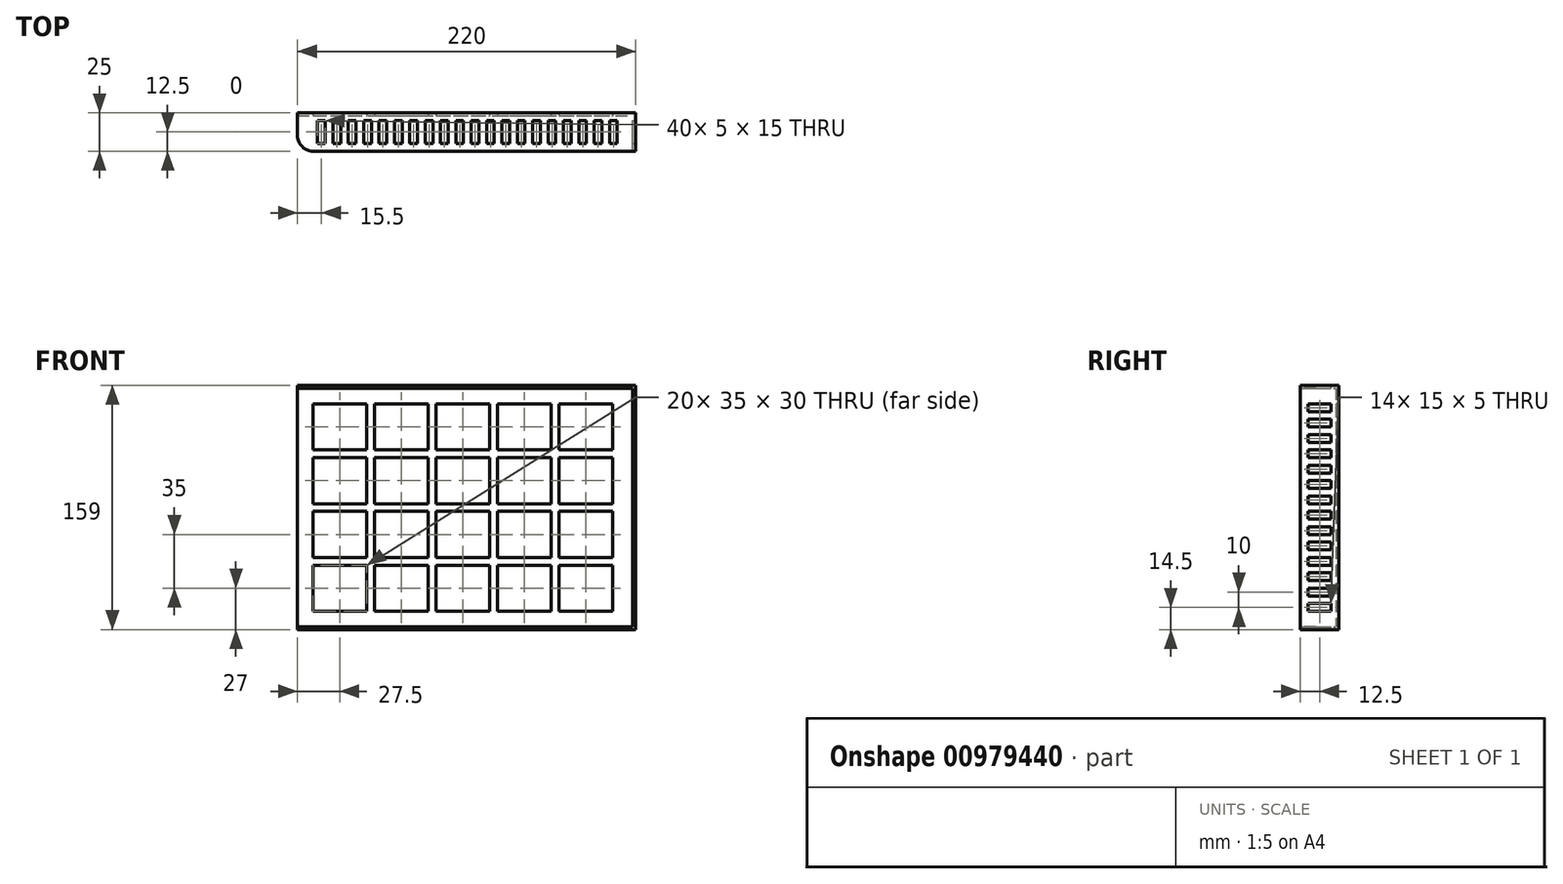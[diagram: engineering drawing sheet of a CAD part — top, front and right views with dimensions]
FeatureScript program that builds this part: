
annotation { "Feature Type Name" : "Feature", "Feature Type Description" : "" }
export const myFeature = defineFeature(function(context is Context, id is Id, definition is map)
    precondition{}
    {
        {
            var Q0;
            Q0=qCreatedBy(makeId("Front.planeOp"),FACE);
            var sketch = newSketch(context, id + "F0", { "sketchPlane" : qUnion([Q0])});
            skLineSegment(sketch, "E0.bottom", {"start": v(-110, 79.5) * mm, "end": v(110, 79.5) * mm});
            skLineSegment(sketch, "E0.top", {"start": v(-110, -79.5) * mm, "end": v(110, -79.5) * mm});
            skLineSegment(sketch, "E0.left", {"start": v(-110, 79.5) * mm, "end": v(-110, -79.5) * mm});
            skLineSegment(sketch, "E0.right", {"start": v(110, 79.5) * mm, "end": v(110, -79.5) * mm});
            skSolve(sketch);
        }
        {
            var Q0;
            Q0 = qSketchRegion(id + "F0", true);
            extrude(context, id + "F1", {"entities" : qUnion([Q0]), "depth" : 25 * mm, "offsetDistance" : 25 * mm});
        }
        {
            var Q0;
            Q0=makeQuery(id+"F1.opExtrude","CAP_FACE",FACE,{"disambiguationData":[OSD([sQuery(id+"F0.wireOp",EDGE,"E0.bottom"),sQuery(id+"F0.wireOp",EDGE,"E0.top"),sQuery(id+"F0.wireOp",EDGE,"E0.left"),sQuery(id+"F0.wireOp",EDGE,"E0.right")])],"isStart":false});
            var Q1;
            Q1=makeQuery(id+"F1.opExtrude","SWEPT_FACE",FACE,{"disambiguationData":[OSD([sQuery(id+"F0.wireOp",EDGE,"E0.left")])]});
            shell(context, id + "F2", {"entities" : qUnion([Q0, Q1]), "thickness" : 2 * mm});
        }
        {
            var Q0;
            {var subQ0=sQuery(id+"F0.wireOp",EDGE,"E0.left");Q0=makeQuery(id+"F2.opShell","OFFSET_EDGE",EDGE,{"disambiguationData":[OSD([subQ0]),TDD([makeQuery(id+"F1.opExtrude","CAP_EDGE",EDGE,{"disambiguationData":[OSD([subQ0])],"isStart":false})])]});}
            fillet(context, id + "F3", {"entities" : qUnion([Q0]), "radius" : 10 * mm, "tangentPropagation" : true, "allowEdgeOverflow" : false});
        }
        {
            var Q0;
            Q0=makeQuery(id+"F1.opExtrude","CAP_EDGE",EDGE,{"disambiguationData":[OSD([sQuery(id+"F0.wireOp",EDGE,"E0.left")])],"isStart":false});
            fillet(context, id + "F4", {"entities" : qUnion([Q0]), "radius" : 10 * mm, "tangentPropagation" : true, "allowEdgeOverflow" : false});
        }
        {
            var Q0;
            Q0=makeQuery(id+"F2.opShell","OFFSET_FACE",FACE,{"disambiguationData":[OSD([sQuery(id+"F0.wireOp",EDGE,"E0.bottom"),sQuery(id+"F0.wireOp",EDGE,"E0.top"),sQuery(id+"F0.wireOp",EDGE,"E0.left"),sQuery(id+"F0.wireOp",EDGE,"E0.right")])]});
            var sketch = newSketch(context, id + "F5", { "sketchPlane" : qUnion([Q0])});
            skLineSegment(sketch, "E1.bottom", {"start": v(-110, 77.5) * mm, "end": v(-100, 77.5) * mm});
            skLineSegment(sketch, "E1.top", {"start": v(-110, 67.5) * mm, "end": v(-100, 67.5) * mm});
            skLineSegment(sketch, "E1.left", {"start": v(-110, 77.5) * mm, "end": v(-110, 67.5) * mm});
            skLineSegment(sketch, "E1.right", {"start": v(-100, 77.5) * mm, "end": v(-100, 67.5) * mm});
            skLineSegment(sketch, "E2.bottom", {"start": v(-100, 67.5) * mm, "end": v(-65, 67.5) * mm});
            skLineSegment(sketch, "E2.top", {"start": v(-100, 37.5) * mm, "end": v(-65, 37.5) * mm});
            skLineSegment(sketch, "E2.left", {"start": v(-100, 67.5) * mm, "end": v(-100, 37.5) * mm});
            skLineSegment(sketch, "E2.right", {"start": v(-65, 67.5) * mm, "end": v(-65, 37.5) * mm});
            skLineSegment(sketch, "E3.0.1.0", {"start": v(-65, 32.5) * mm, "end": v(-65, 2.5) * mm});
            skLineSegment(sketch, "E3.0.1.1", {"start": v(-100, 32.5) * mm, "end": v(-65, 32.5) * mm});
            skLineSegment(sketch, "E3.0.1.2", {"start": v(-100, 32.5) * mm, "end": v(-100, 2.5) * mm});
            skLineSegment(sketch, "E3.0.1.3", {"start": v(-100, 2.5) * mm, "end": v(-65, 2.5) * mm});
            skLineSegment(sketch, "E3.0.2.0", {"start": v(-65, -2.5) * mm, "end": v(-65, -32.5) * mm});
            skLineSegment(sketch, "E3.0.2.1", {"start": v(-100, -2.5) * mm, "end": v(-65, -2.5) * mm});
            skLineSegment(sketch, "E3.0.2.2", {"start": v(-100, -2.5) * mm, "end": v(-100, -32.5) * mm});
            skLineSegment(sketch, "E3.0.2.3", {"start": v(-100, -32.5) * mm, "end": v(-65, -32.5) * mm});
            skLineSegment(sketch, "E3.0.3.0", {"start": v(-65, -37.5) * mm, "end": v(-65, -67.5) * mm});
            skLineSegment(sketch, "E3.0.3.1", {"start": v(-100, -37.5) * mm, "end": v(-65, -37.5) * mm});
            skLineSegment(sketch, "E3.0.3.2", {"start": v(-100, -37.5) * mm, "end": v(-100, -67.5) * mm});
            skLineSegment(sketch, "E3.0.3.3", {"start": v(-100, -67.5) * mm, "end": v(-65, -67.5) * mm});
            skLineSegment(sketch, "E3.1.0.0", {"start": v(-25, 67.5) * mm, "end": v(-25, 37.5) * mm});
            skLineSegment(sketch, "E3.1.0.1", {"start": v(-60, 67.5) * mm, "end": v(-25, 67.5) * mm});
            skLineSegment(sketch, "E3.1.0.2", {"start": v(-60, 67.5) * mm, "end": v(-60, 37.5) * mm});
            skLineSegment(sketch, "E3.1.0.3", {"start": v(-60, 37.5) * mm, "end": v(-25, 37.5) * mm});
            skLineSegment(sketch, "E3.1.1.0", {"start": v(-25, 32.5) * mm, "end": v(-25, 2.5) * mm});
            skLineSegment(sketch, "E3.1.1.1", {"start": v(-60, 32.5) * mm, "end": v(-25, 32.5) * mm});
            skLineSegment(sketch, "E3.1.1.2", {"start": v(-60, 32.5) * mm, "end": v(-60, 2.5) * mm});
            skLineSegment(sketch, "E3.1.1.3", {"start": v(-60, 2.5) * mm, "end": v(-25, 2.5) * mm});
            skLineSegment(sketch, "E3.1.2.0", {"start": v(-25, -2.5) * mm, "end": v(-25, -32.5) * mm});
            skLineSegment(sketch, "E3.1.2.1", {"start": v(-60, -2.5) * mm, "end": v(-25, -2.5) * mm});
            skLineSegment(sketch, "E3.1.2.2", {"start": v(-60, -2.5) * mm, "end": v(-60, -32.5) * mm});
            skLineSegment(sketch, "E3.1.2.3", {"start": v(-60, -32.5) * mm, "end": v(-25, -32.5) * mm});
            skLineSegment(sketch, "E3.1.3.0", {"start": v(-25, -37.5) * mm, "end": v(-25, -67.5) * mm});
            skLineSegment(sketch, "E3.1.3.1", {"start": v(-60, -37.5) * mm, "end": v(-25, -37.5) * mm});
            skLineSegment(sketch, "E3.1.3.2", {"start": v(-60, -37.5) * mm, "end": v(-60, -67.5) * mm});
            skLineSegment(sketch, "E3.1.3.3", {"start": v(-60, -67.5) * mm, "end": v(-25, -67.5) * mm});
            skLineSegment(sketch, "E3.2.0.0", {"start": v(15, 67.5) * mm, "end": v(15, 37.5) * mm});
            skLineSegment(sketch, "E3.2.0.1", {"start": v(-20, 67.5) * mm, "end": v(15, 67.5) * mm});
            skLineSegment(sketch, "E3.2.0.2", {"start": v(-20, 67.5) * mm, "end": v(-20, 37.5) * mm});
            skLineSegment(sketch, "E3.2.0.3", {"start": v(-20, 37.5) * mm, "end": v(15, 37.5) * mm});
            skLineSegment(sketch, "E3.2.1.0", {"start": v(15, 32.5) * mm, "end": v(15, 2.5) * mm});
            skLineSegment(sketch, "E3.2.1.1", {"start": v(-20, 32.5) * mm, "end": v(15, 32.5) * mm});
            skLineSegment(sketch, "E3.2.1.2", {"start": v(-20, 32.5) * mm, "end": v(-20, 2.5) * mm});
            skLineSegment(sketch, "E3.2.1.3", {"start": v(-20, 2.5) * mm, "end": v(15, 2.5) * mm});
            skLineSegment(sketch, "E3.2.2.0", {"start": v(15, -2.5) * mm, "end": v(15, -32.5) * mm});
            skLineSegment(sketch, "E3.2.2.1", {"start": v(-20, -2.5) * mm, "end": v(15, -2.5) * mm});
            skLineSegment(sketch, "E3.2.2.2", {"start": v(-20, -2.5) * mm, "end": v(-20, -32.5) * mm});
            skLineSegment(sketch, "E3.2.2.3", {"start": v(-20, -32.5) * mm, "end": v(15, -32.5) * mm});
            skLineSegment(sketch, "E3.2.3.0", {"start": v(15, -37.5) * mm, "end": v(15, -67.5) * mm});
            skLineSegment(sketch, "E3.2.3.1", {"start": v(-20, -37.5) * mm, "end": v(15, -37.5) * mm});
            skLineSegment(sketch, "E3.2.3.2", {"start": v(-20, -37.5) * mm, "end": v(-20, -67.5) * mm});
            skLineSegment(sketch, "E3.2.3.3", {"start": v(-20, -67.5) * mm, "end": v(15, -67.5) * mm});
            skLineSegment(sketch, "E3.3.0.0", {"start": v(55, 67.5) * mm, "end": v(55, 37.5) * mm});
            skLineSegment(sketch, "E3.3.0.1", {"start": v(20, 67.5) * mm, "end": v(55, 67.5) * mm});
            skLineSegment(sketch, "E3.3.0.2", {"start": v(20, 67.5) * mm, "end": v(20, 37.5) * mm});
            skLineSegment(sketch, "E3.3.0.3", {"start": v(20, 37.5) * mm, "end": v(55, 37.5) * mm});
            skLineSegment(sketch, "E3.3.1.0", {"start": v(55, 32.5) * mm, "end": v(55, 2.5) * mm});
            skLineSegment(sketch, "E3.3.1.1", {"start": v(20, 32.5) * mm, "end": v(55, 32.5) * mm});
            skLineSegment(sketch, "E3.3.1.2", {"start": v(20, 32.5) * mm, "end": v(20, 2.5) * mm});
            skLineSegment(sketch, "E3.3.1.3", {"start": v(20, 2.5) * mm, "end": v(55, 2.5) * mm});
            skLineSegment(sketch, "E3.3.2.0", {"start": v(55, -2.5) * mm, "end": v(55, -32.5) * mm});
            skLineSegment(sketch, "E3.3.2.1", {"start": v(20, -2.5) * mm, "end": v(55, -2.5) * mm});
            skLineSegment(sketch, "E3.3.2.2", {"start": v(20, -2.5) * mm, "end": v(20, -32.5) * mm});
            skLineSegment(sketch, "E3.3.2.3", {"start": v(20, -32.5) * mm, "end": v(55, -32.5) * mm});
            skLineSegment(sketch, "E3.3.3.0", {"start": v(55, -37.5) * mm, "end": v(55, -67.5) * mm});
            skLineSegment(sketch, "E3.3.3.1", {"start": v(20, -37.5) * mm, "end": v(55, -37.5) * mm});
            skLineSegment(sketch, "E3.3.3.2", {"start": v(20, -37.5) * mm, "end": v(20, -67.5) * mm});
            skLineSegment(sketch, "E3.3.3.3", {"start": v(20, -67.5) * mm, "end": v(55, -67.5) * mm});
            skLineSegment(sketch, "E3.4.0.0", {"start": v(95, 67.5) * mm, "end": v(95, 37.5) * mm});
            skLineSegment(sketch, "E3.4.0.1", {"start": v(60, 67.5) * mm, "end": v(95, 67.5) * mm});
            skLineSegment(sketch, "E3.4.0.2", {"start": v(60, 67.5) * mm, "end": v(60, 37.5) * mm});
            skLineSegment(sketch, "E3.4.0.3", {"start": v(60, 37.5) * mm, "end": v(95, 37.5) * mm});
            skLineSegment(sketch, "E3.4.1.0", {"start": v(95, 32.5) * mm, "end": v(95, 2.5) * mm});
            skLineSegment(sketch, "E3.4.1.1", {"start": v(60, 32.5) * mm, "end": v(95, 32.5) * mm});
            skLineSegment(sketch, "E3.4.1.2", {"start": v(60, 32.5) * mm, "end": v(60, 2.5) * mm});
            skLineSegment(sketch, "E3.4.1.3", {"start": v(60, 2.5) * mm, "end": v(95, 2.5) * mm});
            skLineSegment(sketch, "E3.4.2.0", {"start": v(95, -2.5) * mm, "end": v(95, -32.5) * mm});
            skLineSegment(sketch, "E3.4.2.1", {"start": v(60, -2.5) * mm, "end": v(95, -2.5) * mm});
            skLineSegment(sketch, "E3.4.2.2", {"start": v(60, -2.5) * mm, "end": v(60, -32.5) * mm});
            skLineSegment(sketch, "E3.4.2.3", {"start": v(60, -32.5) * mm, "end": v(95, -32.5) * mm});
            skLineSegment(sketch, "E3.4.3.0", {"start": v(95, -37.5) * mm, "end": v(95, -67.5) * mm});
            skLineSegment(sketch, "E3.4.3.1", {"start": v(60, -37.5) * mm, "end": v(95, -37.5) * mm});
            skLineSegment(sketch, "E3.4.3.2", {"start": v(60, -37.5) * mm, "end": v(60, -67.5) * mm});
            skLineSegment(sketch, "E3.4.3.3", {"start": v(60, -67.5) * mm, "end": v(95, -67.5) * mm});
            skLineSegment(sketch, "E3.direction1", {"start": v(-76, 43.5) * mm, "end": v(-36, 43.5) * mm, "construction": true});
            skLineSegment(sketch, "E3.direction2", {"start": v(-76, 43.5) * mm, "end": v(-76, 8.5) * mm, "construction": true});
            skSolve(sketch);
        }
        {
            var Q0;
            Q0=makeQuery(id+"F5.imprint","IMPRINT",FACE,{"disambiguationData":[TD([[makeQuery(id+"F5.imprint","IMPRINT",EDGE,{"derivedFrom":sQuery(id+"F5.wireOp",EDGE,"E2.bottom")}),-1.0]])]});
            var Q1;
            Q1=makeQuery(id+"F5.imprint","IMPRINT",FACE,{"disambiguationData":[TD([[makeQuery(id+"F5.imprint","IMPRINT",EDGE,{"derivedFrom":sQuery(id+"F5.wireOp",EDGE,"E3.1.0.0")}),-1.0]])]});
            var Q2;
            Q2=makeQuery(id+"F5.imprint","IMPRINT",FACE,{"disambiguationData":[TD([[makeQuery(id+"F5.imprint","IMPRINT",EDGE,{"derivedFrom":sQuery(id+"F5.wireOp",EDGE,"E3.2.0.0")}),-1.0]])]});
            var Q3;
            Q3=makeQuery(id+"F5.imprint","IMPRINT",FACE,{"disambiguationData":[TD([[makeQuery(id+"F5.imprint","IMPRINT",EDGE,{"derivedFrom":sQuery(id+"F5.wireOp",EDGE,"E3.3.0.0")}),-1.0]])]});
            var Q4;
            Q4=makeQuery(id+"F5.imprint","IMPRINT",FACE,{"disambiguationData":[TD([[makeQuery(id+"F5.imprint","IMPRINT",EDGE,{"derivedFrom":sQuery(id+"F5.wireOp",EDGE,"E3.4.0.0")}),-1.0]])]});
            var Q5;
            Q5=makeQuery(id+"F5.imprint","IMPRINT",FACE,{"disambiguationData":[TD([[makeQuery(id+"F5.imprint","IMPRINT",EDGE,{"derivedFrom":sQuery(id+"F5.wireOp",EDGE,"E3.4.1.0")}),-1.0]])]});
            var Q6;
            Q6=makeQuery(id+"F5.imprint","IMPRINT",FACE,{"disambiguationData":[TD([[makeQuery(id+"F5.imprint","IMPRINT",EDGE,{"derivedFrom":sQuery(id+"F5.wireOp",EDGE,"E3.3.1.0")}),-1.0]])]});
            var Q7;
            Q7=makeQuery(id+"F5.imprint","IMPRINT",FACE,{"disambiguationData":[TD([[makeQuery(id+"F5.imprint","IMPRINT",EDGE,{"derivedFrom":sQuery(id+"F5.wireOp",EDGE,"E3.2.1.0")}),-1.0]])]});
            var Q8;
            Q8=makeQuery(id+"F5.imprint","IMPRINT",FACE,{"disambiguationData":[TD([[makeQuery(id+"F5.imprint","IMPRINT",EDGE,{"derivedFrom":sQuery(id+"F5.wireOp",EDGE,"E3.1.1.0")}),-1.0]])]});
            var Q9;
            Q9=makeQuery(id+"F5.imprint","IMPRINT",FACE,{"disambiguationData":[TD([[makeQuery(id+"F5.imprint","IMPRINT",EDGE,{"derivedFrom":sQuery(id+"F5.wireOp",EDGE,"E3.0.1.0")}),-1.0]])]});
            var Q10;
            Q10=makeQuery(id+"F5.imprint","IMPRINT",FACE,{"disambiguationData":[TD([[makeQuery(id+"F5.imprint","IMPRINT",EDGE,{"derivedFrom":sQuery(id+"F5.wireOp",EDGE,"E3.0.2.0")}),-1.0]])]});
            var Q11;
            Q11=makeQuery(id+"F5.imprint","IMPRINT",FACE,{"disambiguationData":[TD([[makeQuery(id+"F5.imprint","IMPRINT",EDGE,{"derivedFrom":sQuery(id+"F5.wireOp",EDGE,"E3.2.2.0")}),-1.0]])]});
            var Q12;
            Q12=makeQuery(id+"F5.imprint","IMPRINT",FACE,{"disambiguationData":[TD([[makeQuery(id+"F5.imprint","IMPRINT",EDGE,{"derivedFrom":sQuery(id+"F5.wireOp",EDGE,"E3.3.2.0")}),-1.0]])]});
            var Q13;
            Q13=makeQuery(id+"F5.imprint","IMPRINT",FACE,{"disambiguationData":[TD([[makeQuery(id+"F5.imprint","IMPRINT",EDGE,{"derivedFrom":sQuery(id+"F5.wireOp",EDGE,"E3.4.2.0")}),-1.0]])]});
            var Q14;
            Q14=makeQuery(id+"F5.imprint","IMPRINT",FACE,{"disambiguationData":[TD([[makeQuery(id+"F5.imprint","IMPRINT",EDGE,{"derivedFrom":sQuery(id+"F5.wireOp",EDGE,"E3.4.3.0")}),-1.0]])]});
            var Q15;
            Q15=makeQuery(id+"F5.imprint","IMPRINT",FACE,{"disambiguationData":[TD([[makeQuery(id+"F5.imprint","IMPRINT",EDGE,{"derivedFrom":sQuery(id+"F5.wireOp",EDGE,"E3.3.3.0")}),-1.0]])]});
            var Q16;
            Q16=makeQuery(id+"F5.imprint","IMPRINT",FACE,{"disambiguationData":[TD([[makeQuery(id+"F5.imprint","IMPRINT",EDGE,{"derivedFrom":sQuery(id+"F5.wireOp",EDGE,"E3.1.3.0")}),-1.0]])]});
            var Q17;
            Q17=makeQuery(id+"F5.imprint","IMPRINT",FACE,{"disambiguationData":[TD([[makeQuery(id+"F5.imprint","IMPRINT",EDGE,{"derivedFrom":sQuery(id+"F5.wireOp",EDGE,"E3.0.3.0")}),-1.0]])]});
            var Q18;
            Q18=makeQuery(id+"F5.imprint","IMPRINT",FACE,{"disambiguationData":[TD([[makeQuery(id+"F5.imprint","IMPRINT",EDGE,{"derivedFrom":sQuery(id+"F5.wireOp",EDGE,"E3.1.2.0")}),-1.0]])]});
            var Q19;
            Q19=makeQuery(id+"F5.imprint","IMPRINT",FACE,{"disambiguationData":[TD([[makeQuery(id+"F5.imprint","IMPRINT",EDGE,{"derivedFrom":sQuery(id+"F5.wireOp",EDGE,"E3.2.3.0")}),-1.0]])]});
            extrude(context, id + "F6", {"entities" : qUnion([Q0, Q1, Q2, Q3, Q4, Q5, Q6, Q7, Q8, Q9, Q10, Q11, Q12, Q13, Q14, Q15, Q16, Q17, Q18, Q19]), "operationType" : NewBodyOperationType.REMOVE, "oppositeDirection" : true, "depth" : 25 * mm, "offsetDistance" : 25 * mm});
        }
        {
            var Q0;
            Q0=makeQuery(id+"F1.opExtrude","SWEPT_FACE",FACE,{"disambiguationData":[OSD([sQuery(id+"F0.wireOp",EDGE,"E0.bottom")])]});
            var sketch = newSketch(context, id + "F7", { "sketchPlane" : qUnion([Q0])});
            skLineSegment(sketch, "E4.bottom", {"start": v(98, -20) * mm, "end": v(93, -20) * mm});
            skLineSegment(sketch, "E4.top", {"start": v(98, -5) * mm, "end": v(93, -5) * mm});
            skLineSegment(sketch, "E4.left", {"start": v(98, -20) * mm, "end": v(98, -5) * mm});
            skLineSegment(sketch, "E4.right", {"start": v(93, -20) * mm, "end": v(93, -5) * mm});
            skLineSegment(sketch, "E5.1.0.0", {"start": v(88, -20) * mm, "end": v(83, -20) * mm});
            skLineSegment(sketch, "E5.1.0.1", {"start": v(83, -20) * mm, "end": v(83, -5) * mm});
            skLineSegment(sketch, "E5.1.0.2", {"start": v(88, -20) * mm, "end": v(88, -5) * mm});
            skLineSegment(sketch, "E5.1.0.3", {"start": v(88, -5) * mm, "end": v(83, -5) * mm});
            skLineSegment(sketch, "E5.2.0.0", {"start": v(78, -20) * mm, "end": v(73, -20) * mm});
            skLineSegment(sketch, "E5.2.0.1", {"start": v(73, -20) * mm, "end": v(73, -5) * mm});
            skLineSegment(sketch, "E5.2.0.2", {"start": v(78, -20) * mm, "end": v(78, -5) * mm});
            skLineSegment(sketch, "E5.2.0.3", {"start": v(78, -5) * mm, "end": v(73, -5) * mm});
            skLineSegment(sketch, "E5.3.0.0", {"start": v(68, -20) * mm, "end": v(63, -20) * mm});
            skLineSegment(sketch, "E5.3.0.1", {"start": v(63, -20) * mm, "end": v(63, -5) * mm});
            skLineSegment(sketch, "E5.3.0.2", {"start": v(68, -20) * mm, "end": v(68, -5) * mm});
            skLineSegment(sketch, "E5.3.0.3", {"start": v(68, -5) * mm, "end": v(63, -5) * mm});
            skLineSegment(sketch, "E5.4.0.0", {"start": v(58, -20) * mm, "end": v(53, -20) * mm});
            skLineSegment(sketch, "E5.4.0.1", {"start": v(53, -20) * mm, "end": v(53, -5) * mm});
            skLineSegment(sketch, "E5.4.0.2", {"start": v(58, -20) * mm, "end": v(58, -5) * mm});
            skLineSegment(sketch, "E5.4.0.3", {"start": v(58, -5) * mm, "end": v(53, -5) * mm});
            skLineSegment(sketch, "E5.5.0.0", {"start": v(48, -20) * mm, "end": v(43, -20) * mm});
            skLineSegment(sketch, "E5.5.0.1", {"start": v(43, -20) * mm, "end": v(43, -5) * mm});
            skLineSegment(sketch, "E5.5.0.2", {"start": v(48, -20) * mm, "end": v(48, -5) * mm});
            skLineSegment(sketch, "E5.5.0.3", {"start": v(48, -5) * mm, "end": v(43, -5) * mm});
            skLineSegment(sketch, "E5.6.0.0", {"start": v(38, -20) * mm, "end": v(33, -20) * mm});
            skLineSegment(sketch, "E5.6.0.1", {"start": v(33, -20) * mm, "end": v(33, -5) * mm});
            skLineSegment(sketch, "E5.6.0.2", {"start": v(38, -20) * mm, "end": v(38, -5) * mm});
            skLineSegment(sketch, "E5.6.0.3", {"start": v(38, -5) * mm, "end": v(33, -5) * mm});
            skLineSegment(sketch, "E5.7.0.0", {"start": v(28, -20) * mm, "end": v(23, -20) * mm});
            skLineSegment(sketch, "E5.7.0.1", {"start": v(23, -20) * mm, "end": v(23, -5) * mm});
            skLineSegment(sketch, "E5.7.0.2", {"start": v(28, -20) * mm, "end": v(28, -5) * mm});
            skLineSegment(sketch, "E5.7.0.3", {"start": v(28, -5) * mm, "end": v(23, -5) * mm});
            skLineSegment(sketch, "E5.8.0.0", {"start": v(18, -20) * mm, "end": v(13, -20) * mm});
            skLineSegment(sketch, "E5.8.0.1", {"start": v(13, -20) * mm, "end": v(13, -5) * mm});
            skLineSegment(sketch, "E5.8.0.2", {"start": v(18, -20) * mm, "end": v(18, -5) * mm});
            skLineSegment(sketch, "E5.8.0.3", {"start": v(18, -5) * mm, "end": v(13, -5) * mm});
            skLineSegment(sketch, "E5.9.0.0", {"start": v(8, -20) * mm, "end": v(3, -20) * mm});
            skLineSegment(sketch, "E5.9.0.1", {"start": v(3, -20) * mm, "end": v(3, -5) * mm});
            skLineSegment(sketch, "E5.9.0.2", {"start": v(8, -20) * mm, "end": v(8, -5) * mm});
            skLineSegment(sketch, "E5.9.0.3", {"start": v(8, -5) * mm, "end": v(3, -5) * mm});
            skLineSegment(sketch, "E5.10.0.0", {"start": v(-2, -20) * mm, "end": v(-7, -20) * mm});
            skLineSegment(sketch, "E5.10.0.1", {"start": v(-7, -20) * mm, "end": v(-7, -5) * mm});
            skLineSegment(sketch, "E5.10.0.2", {"start": v(-2, -20) * mm, "end": v(-2, -5) * mm});
            skLineSegment(sketch, "E5.10.0.3", {"start": v(-2, -5) * mm, "end": v(-7, -5) * mm});
            skLineSegment(sketch, "E5.11.0.0", {"start": v(-12, -20) * mm, "end": v(-17, -20) * mm});
            skLineSegment(sketch, "E5.11.0.1", {"start": v(-17, -20) * mm, "end": v(-17, -5) * mm});
            skLineSegment(sketch, "E5.11.0.2", {"start": v(-12, -20) * mm, "end": v(-12, -5) * mm});
            skLineSegment(sketch, "E5.11.0.3", {"start": v(-12, -5) * mm, "end": v(-17, -5) * mm});
            skLineSegment(sketch, "E5.12.0.0", {"start": v(-22, -20) * mm, "end": v(-27, -20) * mm});
            skLineSegment(sketch, "E5.12.0.1", {"start": v(-27, -20) * mm, "end": v(-27, -5) * mm});
            skLineSegment(sketch, "E5.12.0.2", {"start": v(-22, -20) * mm, "end": v(-22, -5) * mm});
            skLineSegment(sketch, "E5.12.0.3", {"start": v(-22, -5) * mm, "end": v(-27, -5) * mm});
            skLineSegment(sketch, "E5.13.0.0", {"start": v(-32, -20) * mm, "end": v(-37, -20) * mm});
            skLineSegment(sketch, "E5.13.0.1", {"start": v(-37, -20) * mm, "end": v(-37, -5) * mm});
            skLineSegment(sketch, "E5.13.0.2", {"start": v(-32, -20) * mm, "end": v(-32, -5) * mm});
            skLineSegment(sketch, "E5.13.0.3", {"start": v(-32, -5) * mm, "end": v(-37, -5) * mm});
            skLineSegment(sketch, "E5.14.0.0", {"start": v(-42, -20) * mm, "end": v(-47, -20) * mm});
            skLineSegment(sketch, "E5.14.0.1", {"start": v(-47, -20) * mm, "end": v(-47, -5) * mm});
            skLineSegment(sketch, "E5.14.0.2", {"start": v(-42, -20) * mm, "end": v(-42, -5) * mm});
            skLineSegment(sketch, "E5.14.0.3", {"start": v(-42, -5) * mm, "end": v(-47, -5) * mm});
            skLineSegment(sketch, "E5.15.0.0", {"start": v(-52, -20) * mm, "end": v(-57, -20) * mm});
            skLineSegment(sketch, "E5.15.0.1", {"start": v(-57, -20) * mm, "end": v(-57, -5) * mm});
            skLineSegment(sketch, "E5.15.0.2", {"start": v(-52, -20) * mm, "end": v(-52, -5) * mm});
            skLineSegment(sketch, "E5.15.0.3", {"start": v(-52, -5) * mm, "end": v(-57, -5) * mm});
            skLineSegment(sketch, "E5.16.0.0", {"start": v(-62, -20) * mm, "end": v(-67, -20) * mm});
            skLineSegment(sketch, "E5.16.0.1", {"start": v(-67, -20) * mm, "end": v(-67, -5) * mm});
            skLineSegment(sketch, "E5.16.0.2", {"start": v(-62, -20) * mm, "end": v(-62, -5) * mm});
            skLineSegment(sketch, "E5.16.0.3", {"start": v(-62, -5) * mm, "end": v(-67, -5) * mm});
            skLineSegment(sketch, "E5.17.0.0", {"start": v(-72, -20) * mm, "end": v(-77, -20) * mm});
            skLineSegment(sketch, "E5.17.0.1", {"start": v(-77, -20) * mm, "end": v(-77, -5) * mm});
            skLineSegment(sketch, "E5.17.0.2", {"start": v(-72, -20) * mm, "end": v(-72, -5) * mm});
            skLineSegment(sketch, "E5.17.0.3", {"start": v(-72, -5) * mm, "end": v(-77, -5) * mm});
            skLineSegment(sketch, "E5.18.0.0", {"start": v(-82, -20) * mm, "end": v(-87, -20) * mm});
            skLineSegment(sketch, "E5.18.0.1", {"start": v(-87, -20) * mm, "end": v(-87, -5) * mm});
            skLineSegment(sketch, "E5.18.0.2", {"start": v(-82, -20) * mm, "end": v(-82, -5) * mm});
            skLineSegment(sketch, "E5.18.0.3", {"start": v(-82, -5) * mm, "end": v(-87, -5) * mm});
            skLineSegment(sketch, "E5.19.0.0", {"start": v(-92, -20) * mm, "end": v(-97, -20) * mm});
            skLineSegment(sketch, "E5.19.0.1", {"start": v(-97, -20) * mm, "end": v(-97, -5) * mm});
            skLineSegment(sketch, "E5.19.0.2", {"start": v(-92, -20) * mm, "end": v(-92, -5) * mm});
            skLineSegment(sketch, "E5.19.0.3", {"start": v(-92, -5) * mm, "end": v(-97, -5) * mm});
            skLineSegment(sketch, "E5.direction1", {"start": v(93, -20) * mm, "end": v(83, -20) * mm, "construction": true});
            skPoint(sketch, "E6.right.end.orphan", {"position": v(98, -5) * mm});
            skSolve(sketch);
        }
        {
            var Q0;
            Q0=makeQuery(id+"F7.imprint","IMPRINT",FACE,{"disambiguationData":[TD([[makeQuery(id+"F7.imprint","IMPRINT",EDGE,{"derivedFrom":sQuery(id+"F7.wireOp",EDGE,"E4.bottom")}),-1.0]])]});
            var Q1;
            Q1=makeQuery(id+"F7.imprint","IMPRINT",FACE,{"disambiguationData":[TD([[makeQuery(id+"F7.imprint","IMPRINT",EDGE,{"derivedFrom":sQuery(id+"F7.wireOp",EDGE,"E5.1.0.0")}),-1.0]])]});
            var Q2;
            Q2=makeQuery(id+"F7.imprint","IMPRINT",FACE,{"disambiguationData":[TD([[makeQuery(id+"F7.imprint","IMPRINT",EDGE,{"derivedFrom":sQuery(id+"F7.wireOp",EDGE,"E5.2.0.0")}),-1.0]])]});
            var Q3;
            Q3=makeQuery(id+"F7.imprint","IMPRINT",FACE,{"disambiguationData":[TD([[makeQuery(id+"F7.imprint","IMPRINT",EDGE,{"derivedFrom":sQuery(id+"F7.wireOp",EDGE,"E5.3.0.0")}),-1.0]])]});
            var Q4;
            Q4=makeQuery(id+"F7.imprint","IMPRINT",FACE,{"disambiguationData":[TD([[makeQuery(id+"F7.imprint","IMPRINT",EDGE,{"derivedFrom":sQuery(id+"F7.wireOp",EDGE,"E5.4.0.0")}),-1.0]])]});
            var Q5;
            Q5=makeQuery(id+"F7.imprint","IMPRINT",FACE,{"disambiguationData":[TD([[makeQuery(id+"F7.imprint","IMPRINT",EDGE,{"derivedFrom":sQuery(id+"F7.wireOp",EDGE,"E5.5.0.0")}),-1.0]])]});
            var Q6;
            Q6=makeQuery(id+"F7.imprint","IMPRINT",FACE,{"disambiguationData":[TD([[makeQuery(id+"F7.imprint","IMPRINT",EDGE,{"derivedFrom":sQuery(id+"F7.wireOp",EDGE,"E5.6.0.0")}),-1.0]])]});
            var Q7;
            Q7=makeQuery(id+"F7.imprint","IMPRINT",FACE,{"disambiguationData":[TD([[makeQuery(id+"F7.imprint","IMPRINT",EDGE,{"derivedFrom":sQuery(id+"F7.wireOp",EDGE,"E5.7.0.0")}),-1.0]])]});
            var Q8;
            Q8=makeQuery(id+"F7.imprint","IMPRINT",FACE,{"disambiguationData":[TD([[makeQuery(id+"F7.imprint","IMPRINT",EDGE,{"derivedFrom":sQuery(id+"F7.wireOp",EDGE,"E5.8.0.0")}),-1.0]])]});
            var Q9;
            Q9=makeQuery(id+"F7.imprint","IMPRINT",FACE,{"disambiguationData":[TD([[makeQuery(id+"F7.imprint","IMPRINT",EDGE,{"derivedFrom":sQuery(id+"F7.wireOp",EDGE,"E5.9.0.0")}),-1.0]])]});
            var Q10;
            Q10=makeQuery(id+"F7.imprint","IMPRINT",FACE,{"disambiguationData":[TD([[makeQuery(id+"F7.imprint","IMPRINT",EDGE,{"derivedFrom":sQuery(id+"F7.wireOp",EDGE,"E5.10.0.0")}),-1.0]])]});
            var Q11;
            Q11=makeQuery(id+"F7.imprint","IMPRINT",FACE,{"disambiguationData":[TD([[makeQuery(id+"F7.imprint","IMPRINT",EDGE,{"derivedFrom":sQuery(id+"F7.wireOp",EDGE,"E5.12.0.0")}),-1.0]])]});
            var Q12;
            Q12=makeQuery(id+"F7.imprint","IMPRINT",FACE,{"disambiguationData":[TD([[makeQuery(id+"F7.imprint","IMPRINT",EDGE,{"derivedFrom":sQuery(id+"F7.wireOp",EDGE,"E5.13.0.0")}),-1.0]])]});
            var Q13;
            Q13=makeQuery(id+"F7.imprint","IMPRINT",FACE,{"disambiguationData":[TD([[makeQuery(id+"F7.imprint","IMPRINT",EDGE,{"derivedFrom":sQuery(id+"F7.wireOp",EDGE,"E5.14.0.0")}),-1.0]])]});
            var Q14;
            Q14=makeQuery(id+"F7.imprint","IMPRINT",FACE,{"disambiguationData":[TD([[makeQuery(id+"F7.imprint","IMPRINT",EDGE,{"derivedFrom":sQuery(id+"F7.wireOp",EDGE,"E5.15.0.0")}),-1.0]])]});
            var Q15;
            Q15=makeQuery(id+"F7.imprint","IMPRINT",FACE,{"disambiguationData":[TD([[makeQuery(id+"F7.imprint","IMPRINT",EDGE,{"derivedFrom":sQuery(id+"F7.wireOp",EDGE,"E5.16.0.0")}),-1.0]])]});
            var Q16;
            Q16=makeQuery(id+"F7.imprint","IMPRINT",FACE,{"disambiguationData":[TD([[makeQuery(id+"F7.imprint","IMPRINT",EDGE,{"derivedFrom":sQuery(id+"F7.wireOp",EDGE,"E5.17.0.0")}),-1.0]])]});
            var Q17;
            Q17=makeQuery(id+"F7.imprint","IMPRINT",FACE,{"disambiguationData":[TD([[makeQuery(id+"F7.imprint","IMPRINT",EDGE,{"derivedFrom":sQuery(id+"F7.wireOp",EDGE,"E5.18.0.0")}),-1.0]])]});
            var Q18;
            Q18=makeQuery(id+"F7.imprint","IMPRINT",FACE,{"disambiguationData":[TD([[makeQuery(id+"F7.imprint","IMPRINT",EDGE,{"derivedFrom":sQuery(id+"F7.wireOp",EDGE,"E5.19.0.0")}),-1.0]])]});
            var Q19;
            Q19=makeQuery(id+"F7.imprint","IMPRINT",FACE,{"disambiguationData":[TD([[makeQuery(id+"F7.imprint","IMPRINT",EDGE,{"derivedFrom":sQuery(id+"F7.wireOp",EDGE,"E5.11.0.0")}),-1.0]])]});
            extrude(context, id + "F8", {"entities" : qUnion([Q0, Q1, Q2, Q3, Q4, Q5, Q6, Q7, Q8, Q9, Q10, Q11, Q12, Q13, Q14, Q15, Q16, Q17, Q18, Q19]), "operationType" : NewBodyOperationType.REMOVE, "endBound" : BoundingType.THROUGH_ALL, "oppositeDirection" : true, "depth" : 25 * mm, "offsetDistance" : 25 * mm});
        }
        {
            var Q0;
            Q0=makeQuery(id+"F1.opExtrude","SWEPT_FACE",FACE,{"disambiguationData":[OSD([sQuery(id+"F0.wireOp",EDGE,"E0.right")])]});
            var sketch = newSketch(context, id + "F9", { "sketchPlane" : qUnion([Q0])});
            skLineSegment(sketch, "E7.bottom", {"start": v(-20, 67.5) * mm, "end": v(-5, 67.5) * mm});
            skLineSegment(sketch, "E7.top", {"start": v(-20, 62.5) * mm, "end": v(-5, 62.5) * mm});
            skLineSegment(sketch, "E7.left", {"start": v(-20, 67.5) * mm, "end": v(-20, 62.5) * mm});
            skLineSegment(sketch, "E7.right", {"start": v(-5, 67.5) * mm, "end": v(-5, 62.5) * mm});
            skLineSegment(sketch, "E8.0.1.0", {"start": v(-20, 52.5) * mm, "end": v(-5, 52.5) * mm});
            skLineSegment(sketch, "E8.0.1.1", {"start": v(-5, 57.5) * mm, "end": v(-5, 52.5) * mm});
            skLineSegment(sketch, "E8.0.1.2", {"start": v(-20, 57.5) * mm, "end": v(-5, 57.5) * mm});
            skLineSegment(sketch, "E8.0.1.3", {"start": v(-20, 57.5) * mm, "end": v(-20, 52.5) * mm});
            skLineSegment(sketch, "E8.0.2.0", {"start": v(-20, 42.5) * mm, "end": v(-5, 42.5) * mm});
            skLineSegment(sketch, "E8.0.2.1", {"start": v(-5, 47.5) * mm, "end": v(-5, 42.5) * mm});
            skLineSegment(sketch, "E8.0.2.2", {"start": v(-20, 47.5) * mm, "end": v(-5, 47.5) * mm});
            skLineSegment(sketch, "E8.0.2.3", {"start": v(-20, 47.5) * mm, "end": v(-20, 42.5) * mm});
            skLineSegment(sketch, "E8.0.3.0", {"start": v(-20, 32.5) * mm, "end": v(-5, 32.5) * mm});
            skLineSegment(sketch, "E8.0.3.1", {"start": v(-5, 37.5) * mm, "end": v(-5, 32.5) * mm});
            skLineSegment(sketch, "E8.0.3.2", {"start": v(-20, 37.5) * mm, "end": v(-5, 37.5) * mm});
            skLineSegment(sketch, "E8.0.3.3", {"start": v(-20, 37.5) * mm, "end": v(-20, 32.5) * mm});
            skLineSegment(sketch, "E8.0.4.0", {"start": v(-20, 22.5) * mm, "end": v(-5, 22.5) * mm});
            skLineSegment(sketch, "E8.0.4.1", {"start": v(-5, 27.5) * mm, "end": v(-5, 22.5) * mm});
            skLineSegment(sketch, "E8.0.4.2", {"start": v(-20, 27.5) * mm, "end": v(-5, 27.5) * mm});
            skLineSegment(sketch, "E8.0.4.3", {"start": v(-20, 27.5) * mm, "end": v(-20, 22.5) * mm});
            skLineSegment(sketch, "E8.0.5.0", {"start": v(-20, 12.5) * mm, "end": v(-5, 12.5) * mm});
            skLineSegment(sketch, "E8.0.5.1", {"start": v(-5, 17.5) * mm, "end": v(-5, 12.5) * mm});
            skLineSegment(sketch, "E8.0.5.2", {"start": v(-20, 17.5) * mm, "end": v(-5, 17.5) * mm});
            skLineSegment(sketch, "E8.0.5.3", {"start": v(-20, 17.5) * mm, "end": v(-20, 12.5) * mm});
            skLineSegment(sketch, "E8.0.6.0", {"start": v(-20, 2.5) * mm, "end": v(-5, 2.5) * mm});
            skLineSegment(sketch, "E8.0.6.1", {"start": v(-5, 7.5) * mm, "end": v(-5, 2.5) * mm});
            skLineSegment(sketch, "E8.0.6.2", {"start": v(-20, 7.5) * mm, "end": v(-5, 7.5) * mm});
            skLineSegment(sketch, "E8.0.6.3", {"start": v(-20, 7.5) * mm, "end": v(-20, 2.5) * mm});
            skLineSegment(sketch, "E8.0.7.0", {"start": v(-20, -7.5) * mm, "end": v(-5, -7.5) * mm});
            skLineSegment(sketch, "E8.0.7.1", {"start": v(-5, -2.5) * mm, "end": v(-5, -7.5) * mm});
            skLineSegment(sketch, "E8.0.7.2", {"start": v(-20, -2.5) * mm, "end": v(-5, -2.5) * mm});
            skLineSegment(sketch, "E8.0.7.3", {"start": v(-20, -2.5) * mm, "end": v(-20, -7.5) * mm});
            skLineSegment(sketch, "E8.0.8.0", {"start": v(-20, -17.5) * mm, "end": v(-5, -17.5) * mm});
            skLineSegment(sketch, "E8.0.8.1", {"start": v(-5, -12.5) * mm, "end": v(-5, -17.5) * mm});
            skLineSegment(sketch, "E8.0.8.2", {"start": v(-20, -12.5) * mm, "end": v(-5, -12.5) * mm});
            skLineSegment(sketch, "E8.0.8.3", {"start": v(-20, -12.5) * mm, "end": v(-20, -17.5) * mm});
            skLineSegment(sketch, "E8.0.9.0", {"start": v(-20, -27.5) * mm, "end": v(-5, -27.5) * mm});
            skLineSegment(sketch, "E8.0.9.1", {"start": v(-5, -22.5) * mm, "end": v(-5, -27.5) * mm});
            skLineSegment(sketch, "E8.0.9.2", {"start": v(-20, -22.5) * mm, "end": v(-5, -22.5) * mm});
            skLineSegment(sketch, "E8.0.9.3", {"start": v(-20, -22.5) * mm, "end": v(-20, -27.5) * mm});
            skLineSegment(sketch, "E8.0.10.0", {"start": v(-20, -37.5) * mm, "end": v(-5, -37.5) * mm});
            skLineSegment(sketch, "E8.0.10.1", {"start": v(-5, -32.5) * mm, "end": v(-5, -37.5) * mm});
            skLineSegment(sketch, "E8.0.10.2", {"start": v(-20, -32.5) * mm, "end": v(-5, -32.5) * mm});
            skLineSegment(sketch, "E8.0.10.3", {"start": v(-20, -32.5) * mm, "end": v(-20, -37.5) * mm});
            skLineSegment(sketch, "E8.0.11.0", {"start": v(-20, -47.5) * mm, "end": v(-5, -47.5) * mm});
            skLineSegment(sketch, "E8.0.11.1", {"start": v(-5, -42.5) * mm, "end": v(-5, -47.5) * mm});
            skLineSegment(sketch, "E8.0.11.2", {"start": v(-20, -42.5) * mm, "end": v(-5, -42.5) * mm});
            skLineSegment(sketch, "E8.0.11.3", {"start": v(-20, -42.5) * mm, "end": v(-20, -47.5) * mm});
            skLineSegment(sketch, "E8.0.12.0", {"start": v(-20, -57.5) * mm, "end": v(-5, -57.5) * mm});
            skLineSegment(sketch, "E8.0.12.1", {"start": v(-5, -52.5) * mm, "end": v(-5, -57.5) * mm});
            skLineSegment(sketch, "E8.0.12.2", {"start": v(-20, -52.5) * mm, "end": v(-5, -52.5) * mm});
            skLineSegment(sketch, "E8.0.12.3", {"start": v(-20, -52.5) * mm, "end": v(-20, -57.5) * mm});
            skLineSegment(sketch, "E8.0.13.0", {"start": v(-20, -67.5) * mm, "end": v(-5, -67.5) * mm});
            skLineSegment(sketch, "E8.0.13.1", {"start": v(-5, -62.5) * mm, "end": v(-5, -67.5) * mm});
            skLineSegment(sketch, "E8.0.13.2", {"start": v(-20, -62.5) * mm, "end": v(-5, -62.5) * mm});
            skLineSegment(sketch, "E8.0.13.3", {"start": v(-20, -62.5) * mm, "end": v(-20, -67.5) * mm});
            skLineSegment(sketch, "E8.direction1", {"start": v(-20, 62.5) * mm, "end": v(5, 62.5) * mm, "construction": true});
            skLineSegment(sketch, "E8.direction2", {"start": v(-20, 62.5) * mm, "end": v(-20, 52.5) * mm, "construction": true});
            skPoint(sketch, "E9.right.end.orphan", {"position": v(-5, 67.5) * mm});
            skSolve(sketch);
        }
        {
            var Q0;
            Q0=makeQuery(id+"F9.imprint","IMPRINT",FACE,{"disambiguationData":[TD([[makeQuery(id+"F9.imprint","IMPRINT",EDGE,{"derivedFrom":sQuery(id+"F9.wireOp",EDGE,"E7.bottom")}),-1.0]])]});
            var Q1;
            Q1=makeQuery(id+"F9.imprint","IMPRINT",FACE,{"disambiguationData":[TD([[makeQuery(id+"F9.imprint","IMPRINT",EDGE,{"derivedFrom":sQuery(id+"F9.wireOp",EDGE,"E8.0.1.0")}),1.0]])]});
            var Q2;
            Q2=makeQuery(id+"F9.imprint","IMPRINT",FACE,{"disambiguationData":[TD([[makeQuery(id+"F9.imprint","IMPRINT",EDGE,{"derivedFrom":sQuery(id+"F9.wireOp",EDGE,"E8.0.2.0")}),1.0]])]});
            var Q3;
            Q3=makeQuery(id+"F9.imprint","IMPRINT",FACE,{"disambiguationData":[TD([[makeQuery(id+"F9.imprint","IMPRINT",EDGE,{"derivedFrom":sQuery(id+"F9.wireOp",EDGE,"E8.0.3.0")}),1.0]])]});
            var Q4;
            Q4=makeQuery(id+"F9.imprint","IMPRINT",FACE,{"disambiguationData":[TD([[makeQuery(id+"F9.imprint","IMPRINT",EDGE,{"derivedFrom":sQuery(id+"F9.wireOp",EDGE,"E8.0.4.0")}),1.0]])]});
            var Q5;
            Q5=makeQuery(id+"F9.imprint","IMPRINT",FACE,{"disambiguationData":[TD([[makeQuery(id+"F9.imprint","IMPRINT",EDGE,{"derivedFrom":sQuery(id+"F9.wireOp",EDGE,"E8.0.5.0")}),1.0]])]});
            var Q6;
            Q6=makeQuery(id+"F9.imprint","IMPRINT",FACE,{"disambiguationData":[TD([[makeQuery(id+"F9.imprint","IMPRINT",EDGE,{"derivedFrom":sQuery(id+"F9.wireOp",EDGE,"E8.0.6.0")}),1.0]])]});
            var Q7;
            Q7=makeQuery(id+"F9.imprint","IMPRINT",FACE,{"disambiguationData":[TD([[makeQuery(id+"F9.imprint","IMPRINT",EDGE,{"derivedFrom":sQuery(id+"F9.wireOp",EDGE,"E8.0.7.0")}),1.0]])]});
            var Q8;
            Q8=makeQuery(id+"F9.imprint","IMPRINT",FACE,{"disambiguationData":[TD([[makeQuery(id+"F9.imprint","IMPRINT",EDGE,{"derivedFrom":sQuery(id+"F9.wireOp",EDGE,"E8.0.8.0")}),1.0]])]});
            var Q9;
            Q9=makeQuery(id+"F9.imprint","IMPRINT",FACE,{"disambiguationData":[TD([[makeQuery(id+"F9.imprint","IMPRINT",EDGE,{"derivedFrom":sQuery(id+"F9.wireOp",EDGE,"E8.0.9.0")}),1.0]])]});
            var Q10;
            Q10=makeQuery(id+"F9.imprint","IMPRINT",FACE,{"disambiguationData":[TD([[makeQuery(id+"F9.imprint","IMPRINT",EDGE,{"derivedFrom":sQuery(id+"F9.wireOp",EDGE,"E8.0.10.0")}),1.0]])]});
            var Q11;
            Q11=makeQuery(id+"F9.imprint","IMPRINT",FACE,{"disambiguationData":[TD([[makeQuery(id+"F9.imprint","IMPRINT",EDGE,{"derivedFrom":sQuery(id+"F9.wireOp",EDGE,"E8.0.11.0")}),1.0]])]});
            var Q12;
            Q12=makeQuery(id+"F9.imprint","IMPRINT",FACE,{"disambiguationData":[TD([[makeQuery(id+"F9.imprint","IMPRINT",EDGE,{"derivedFrom":sQuery(id+"F9.wireOp",EDGE,"E8.0.12.0")}),1.0]])]});
            var Q13;
            Q13=makeQuery(id+"F9.imprint","IMPRINT",FACE,{"disambiguationData":[TD([[makeQuery(id+"F9.imprint","IMPRINT",EDGE,{"derivedFrom":sQuery(id+"F9.wireOp",EDGE,"E8.0.13.0")}),1.0]])]});
            extrude(context, id + "F10", {"entities" : qUnion([Q0, Q1, Q2, Q3, Q4, Q5, Q6, Q7, Q8, Q9, Q10, Q11, Q12, Q13]), "operationType" : NewBodyOperationType.REMOVE, "oppositeDirection" : true, "depth" : 25 * mm, "offsetDistance" : 25 * mm});
        }
    });
